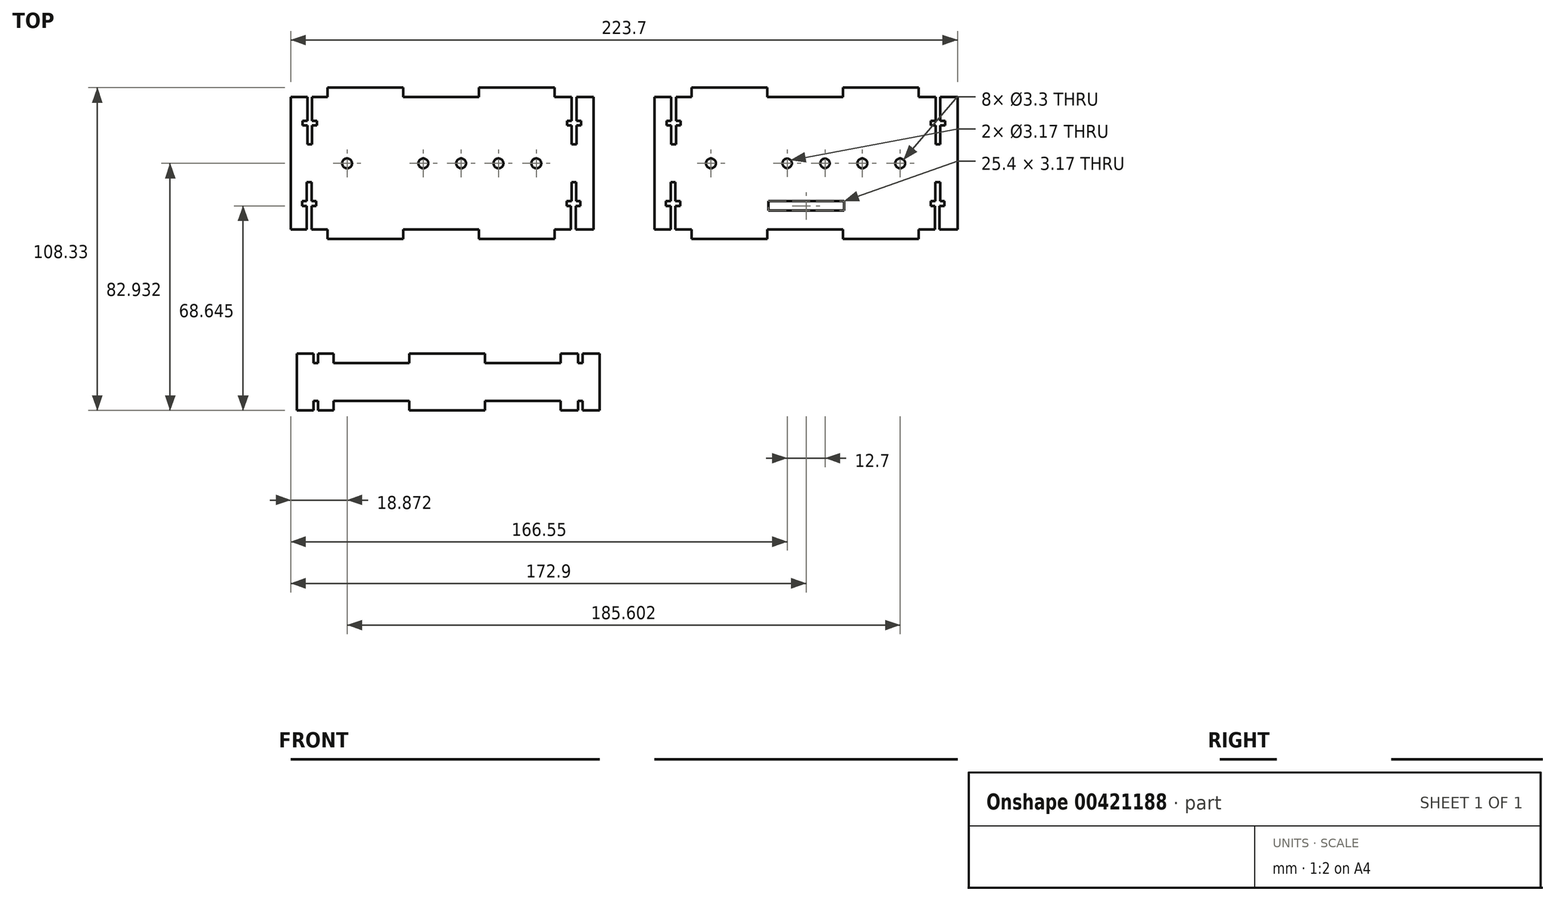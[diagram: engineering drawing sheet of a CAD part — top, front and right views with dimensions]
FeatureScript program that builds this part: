
annotation { "Feature Type Name" : "Feature", "Feature Type Description" : "" }
export const myFeature = defineFeature(function(context is Context, id is Id, definition is map)
    precondition{}
    {
        {
            var Q0;
            Q0=qCreatedBy(makeId("Top.planeOp"),FACE);
            var sketch = newSketch(context, id + "F0", { "sketchPlane" : qUnion([Q0])});
            skCircle(sketch, "E0", {"center": v(26.52, -0.26) * mm, "radius": 1.65 * mm});
            skCircle(sketch, "E1", {"center": v(90.02, -0.26) * mm, "radius": 1.65 * mm});
            skCircle(sketch, "E2", {"center": v(77.32, -0.26) * mm, "radius": 1.65 * mm});
            skLineSegment(sketch, "E3", {"start": v(19.98, -22.48) * mm, "end": v(19.98, -25.66) * mm});
            skLineSegment(sketch, "E4", {"start": v(19.98, -25.66) * mm, "end": v(45.38, -25.66) * mm});
            skLineSegment(sketch, "E5", {"start": v(70.78, -22.48) * mm, "end": v(70.78, -25.66) * mm});
            skLineSegment(sketch, "E6", {"start": v(70.78, -25.66) * mm, "end": v(96.18, -25.66) * mm});
            skLineSegment(sketch, "E7", {"start": v(45.38, -25.66) * mm, "end": v(45.38, -22.48) * mm});
            skLineSegment(sketch, "E8", {"start": v(96.18, -25.66) * mm, "end": v(96.18, -22.48) * mm});
            skLineSegment(sketch, "E9", {"start": v(7.65, -22.48) * mm, "end": v(7.65, 21.97) * mm});
            skLineSegment(sketch, "E10", {"start": v(109.25, 21.97) * mm, "end": v(109.25, -22.48) * mm});
            skLineSegment(sketch, "E11", {"start": v(45.38, 25.14) * mm, "end": v(19.98, 25.14) * mm});
            skLineSegment(sketch, "E12", {"start": v(70.78, 21.97) * mm, "end": v(70.78, 25.14) * mm});
            skLineSegment(sketch, "E13", {"start": v(70.78, 25.14) * mm, "end": v(96.18, 25.14) * mm});
            skLineSegment(sketch, "E14", {"start": v(96.18, 25.14) * mm, "end": v(96.18, 21.97) * mm});
            skLineSegment(sketch, "E15", {"start": v(45.38, 25.14) * mm, "end": v(45.38, 21.97) * mm});
            skLineSegment(sketch, "E16", {"start": v(19.98, 25.14) * mm, "end": v(19.98, 21.97) * mm});
            skLineSegment(sketch, "E17", {"start": v(45.38, -22.48) * mm, "end": v(70.78, -22.48) * mm});
            skLineSegment(sketch, "E18", {"start": v(70.78, 21.97) * mm, "end": v(45.38, 21.97) * mm});
            skLineSegment(sketch, "E19", {"start": v(13.2, 6.1) * mm, "end": v(14.8, 6.1) * mm});
            skLineSegment(sketch, "E20", {"start": v(13.2, 21.97) * mm, "end": v(7.65, 21.97) * mm});
            skLineSegment(sketch, "E21", {"start": v(14.8, 21.97) * mm, "end": v(19.98, 21.97) * mm});
            skLineSegment(sketch, "E22", {"start": v(16.38, 12.44) * mm, "end": v(16.38, 14.03) * mm});
            skLineSegment(sketch, "E23", {"start": v(11.62, 14.03) * mm, "end": v(11.62, 12.44) * mm});
            skLineSegment(sketch, "E24", {"start": v(11.62, 14.03) * mm, "end": v(13.2, 14.03) * mm});
            skLineSegment(sketch, "E25", {"start": v(16.38, 14.03) * mm, "end": v(14.8, 14.03) * mm});
            skLineSegment(sketch, "E26", {"start": v(16.38, 12.44) * mm, "end": v(14.8, 12.44) * mm});
            skLineSegment(sketch, "E27", {"start": v(11.62, 12.44) * mm, "end": v(13.2, 12.44) * mm});
            skLineSegment(sketch, "E28", {"start": v(13.2, 12.44) * mm, "end": v(13.2, 6.1) * mm});
            skLineSegment(sketch, "E29", {"start": v(13.2, 21.97) * mm, "end": v(13.2, 14.03) * mm});
            skLineSegment(sketch, "E30", {"start": v(14.8, 21.97) * mm, "end": v(14.8, 14.03) * mm});
            skLineSegment(sketch, "E31", {"start": v(14.8, 6.1) * mm, "end": v(14.8, 12.44) * mm});
            skLineSegment(sketch, "E32", {"start": v(103.52, 21.97) * mm, "end": v(103.52, 14.03) * mm});
            skLineSegment(sketch, "E33", {"start": v(103.52, 14.03) * mm, "end": v(105.1, 14.03) * mm});
            skLineSegment(sketch, "E34", {"start": v(105.1, 14.03) * mm, "end": v(105.1, 12.44) * mm});
            skLineSegment(sketch, "E35", {"start": v(105.1, 12.44) * mm, "end": v(103.52, 12.44) * mm});
            skLineSegment(sketch, "E36", {"start": v(103.52, 12.44) * mm, "end": v(103.52, 6.1) * mm});
            skLineSegment(sketch, "E37", {"start": v(103.52, 14.03) * mm, "end": v(103.52, 21.97) * mm});
            skLineSegment(sketch, "E38.top", {"start": v(103.52, 6.1) * mm, "end": v(101.93, 6.1) * mm});
            skLineSegment(sketch, "E39.bottom", {"start": v(101.93, 14.03) * mm, "end": v(100.34, 14.03) * mm});
            skLineSegment(sketch, "E39.top", {"start": v(101.93, 12.44) * mm, "end": v(100.34, 12.44) * mm});
            skLineSegment(sketch, "E39.right", {"start": v(100.34, 14.03) * mm, "end": v(100.34, 12.44) * mm});
            skLineSegment(sketch, "E40", {"start": v(101.93, 14.03) * mm, "end": v(101.93, 21.97) * mm});
            skLineSegment(sketch, "E41", {"start": v(101.93, 12.44) * mm, "end": v(101.93, 6.1) * mm});
            skLineSegment(sketch, "E42", {"start": v(103.24, -14.55) * mm, "end": v(104.82, -14.55) * mm});
            skLineSegment(sketch, "E43", {"start": v(104.82, -14.55) * mm, "end": v(104.82, -12.96) * mm});
            skLineSegment(sketch, "E44", {"start": v(104.82, -12.96) * mm, "end": v(103.43, -12.96) * mm});
            skLineSegment(sketch, "E45.bottom", {"start": v(103.43, -6.6) * mm, "end": v(101.84, -6.6) * mm});
            skLineSegment(sketch, "E46.bottom", {"start": v(101.84, -12.96) * mm, "end": v(100.25, -12.96) * mm});
            skLineSegment(sketch, "E46.top", {"start": v(101.65, -14.55) * mm, "end": v(100.25, -14.55) * mm});
            skLineSegment(sketch, "E46.right", {"start": v(100.25, -12.96) * mm, "end": v(100.25, -14.55) * mm});
            skLineSegment(sketch, "E47", {"start": v(101.84, -6.6) * mm, "end": v(101.84, -12.96) * mm});
            skLineSegment(sketch, "E48", {"start": v(103.43, -6.6) * mm, "end": v(103.43, -12.96) * mm});
            skLineSegment(sketch, "E49", {"start": v(103.24, -14.55) * mm, "end": v(103.24, -22.48) * mm});
            skLineSegment(sketch, "E50", {"start": v(101.65, -14.55) * mm, "end": v(101.65, -22.48) * mm});
            skLineSegment(sketch, "E51.top", {"start": v(13.82, -6.6) * mm, "end": v(14.61, -6.6) * mm});
            skLineSegment(sketch, "E52.bottom", {"start": v(14.61, -6.6) * mm, "end": v(13.02, -6.6) * mm});
            skLineSegment(sketch, "E53", {"start": v(13.02, -22.48) * mm, "end": v(7.65, -22.48) * mm});
            skLineSegment(sketch, "E54", {"start": v(14.61, -22.48) * mm, "end": v(19.98, -22.48) * mm});
            skLineSegment(sketch, "E55", {"start": v(14.61, -14.55) * mm, "end": v(16.2, -14.55) * mm});
            skLineSegment(sketch, "E56", {"start": v(16.2, -14.55) * mm, "end": v(16.2, -12.96) * mm});
            skLineSegment(sketch, "E57", {"start": v(16.2, -12.96) * mm, "end": v(14.61, -12.96) * mm});
            skLineSegment(sketch, "E58", {"start": v(13.02, -12.96) * mm, "end": v(11.44, -12.96) * mm});
            skLineSegment(sketch, "E59", {"start": v(11.44, -12.96) * mm, "end": v(11.44, -14.55) * mm});
            skLineSegment(sketch, "E60", {"start": v(11.44, -14.55) * mm, "end": v(13.02, -14.55) * mm});
            skLineSegment(sketch, "E61", {"start": v(13.02, -6.6) * mm, "end": v(13.02, -12.96) * mm});
            skLineSegment(sketch, "E62", {"start": v(14.61, -6.6) * mm, "end": v(14.61, -12.96) * mm});
            skLineSegment(sketch, "E63", {"start": v(14.61, -14.55) * mm, "end": v(14.61, -22.48) * mm});
            skLineSegment(sketch, "E64", {"start": v(13.02, -14.55) * mm, "end": v(13.02, -22.48) * mm});
            skLineSegment(sketch, "E65", {"start": v(96.18, -22.48) * mm, "end": v(101.65, -22.48) * mm});
            skLineSegment(sketch, "E66", {"start": v(103.24, -22.48) * mm, "end": v(109.25, -22.48) * mm});
            skPoint(sketch, "E67.endSnap0", {"position": v(70.78, 23.55) * mm});
            skLineSegment(sketch, "E68", {"start": v(45.75, -12.96) * mm, "end": v(71.15, -12.96) * mm});
            skLineSegment(sketch, "E69", {"start": v(71.15, -12.96) * mm, "end": v(71.15, -16.13) * mm});
            skLineSegment(sketch, "E70", {"start": v(45.75, -12.96) * mm, "end": v(45.75, -16.13) * mm});
            skLineSegment(sketch, "E71", {"start": v(45.75, -16.13) * mm, "end": v(71.15, -16.13) * mm});
            skCircle(sketch, "E72", {"center": v(-95.58, -0.26) * mm, "radius": 1.65 * mm});
            skCircle(sketch, "E73", {"center": v(-32.08, -0.26) * mm, "radius": 1.65 * mm});
            skCircle(sketch, "E74", {"center": v(-44.78, -0.26) * mm, "radius": 1.65 * mm});
            skLineSegment(sketch, "E75", {"start": v(-102.12, -22.48) * mm, "end": v(-102.12, -25.66) * mm});
            skLineSegment(sketch, "E76", {"start": v(-102.12, -25.66) * mm, "end": v(-76.72, -25.66) * mm});
            skLineSegment(sketch, "E77", {"start": v(-51.32, -22.48) * mm, "end": v(-51.32, -25.66) * mm});
            skLineSegment(sketch, "E78", {"start": v(-51.32, -25.66) * mm, "end": v(-25.92, -25.66) * mm});
            skLineSegment(sketch, "E79", {"start": v(-76.72, -25.66) * mm, "end": v(-76.72, -22.48) * mm});
            skLineSegment(sketch, "E80", {"start": v(-25.92, -25.66) * mm, "end": v(-25.92, -22.48) * mm});
            skLineSegment(sketch, "E81", {"start": v(-114.45, -22.48) * mm, "end": v(-114.45, 21.97) * mm});
            skLineSegment(sketch, "E82", {"start": v(-12.85, 21.97) * mm, "end": v(-12.85, -22.48) * mm});
            skLineSegment(sketch, "E83", {"start": v(-76.72, 25.14) * mm, "end": v(-102.12, 25.14) * mm});
            skLineSegment(sketch, "E84", {"start": v(-51.32, 21.97) * mm, "end": v(-51.32, 25.14) * mm});
            skLineSegment(sketch, "E85", {"start": v(-51.32, 25.14) * mm, "end": v(-25.92, 25.14) * mm});
            skLineSegment(sketch, "E86", {"start": v(-25.92, 25.14) * mm, "end": v(-25.92, 21.97) * mm});
            skLineSegment(sketch, "E87", {"start": v(-76.72, 25.14) * mm, "end": v(-76.72, 21.97) * mm});
            skLineSegment(sketch, "E88", {"start": v(-102.12, 25.14) * mm, "end": v(-102.12, 21.97) * mm});
            skLineSegment(sketch, "E89", {"start": v(-76.72, -22.48) * mm, "end": v(-51.32, -22.48) * mm});
            skLineSegment(sketch, "E90", {"start": v(-51.32, 21.97) * mm, "end": v(-76.72, 21.97) * mm});
            skLineSegment(sketch, "E91", {"start": v(-108.9, 6.1) * mm, "end": v(-107.3, 6.1) * mm});
            skLineSegment(sketch, "E92", {"start": v(-108.9, 21.97) * mm, "end": v(-114.45, 21.97) * mm});
            skLineSegment(sketch, "E93", {"start": v(-107.3, 21.97) * mm, "end": v(-102.12, 21.97) * mm});
            skLineSegment(sketch, "E94", {"start": v(-105.72, 12.44) * mm, "end": v(-105.72, 14.03) * mm});
            skLineSegment(sketch, "E95", {"start": v(-110.48, 14.03) * mm, "end": v(-110.48, 12.44) * mm});
            skLineSegment(sketch, "E96", {"start": v(-110.48, 14.03) * mm, "end": v(-108.9, 14.03) * mm});
            skLineSegment(sketch, "E97", {"start": v(-105.72, 14.03) * mm, "end": v(-107.3, 14.03) * mm});
            skLineSegment(sketch, "E98", {"start": v(-105.72, 12.44) * mm, "end": v(-107.3, 12.44) * mm});
            skLineSegment(sketch, "E99", {"start": v(-110.48, 12.44) * mm, "end": v(-108.9, 12.44) * mm});
            skLineSegment(sketch, "E100", {"start": v(-108.9, 12.44) * mm, "end": v(-108.9, 6.1) * mm});
            skLineSegment(sketch, "E101", {"start": v(-108.9, 21.97) * mm, "end": v(-108.9, 14.03) * mm});
            skLineSegment(sketch, "E102", {"start": v(-107.3, 21.97) * mm, "end": v(-107.3, 14.03) * mm});
            skLineSegment(sketch, "E103", {"start": v(-107.3, 6.1) * mm, "end": v(-107.3, 12.44) * mm});
            skLineSegment(sketch, "E104", {"start": v(-18.58, 21.97) * mm, "end": v(-18.58, 14.03) * mm});
            skLineSegment(sketch, "E105", {"start": v(-18.58, 14.03) * mm, "end": v(-17, 14.03) * mm});
            skLineSegment(sketch, "E106", {"start": v(-17, 14.03) * mm, "end": v(-17, 12.44) * mm});
            skLineSegment(sketch, "E107", {"start": v(-17, 12.44) * mm, "end": v(-18.58, 12.44) * mm});
            skLineSegment(sketch, "E108", {"start": v(-18.58, 12.44) * mm, "end": v(-18.58, 6.1) * mm});
            skLineSegment(sketch, "E109", {"start": v(-18.58, 14.03) * mm, "end": v(-18.58, 21.97) * mm});
            skLineSegment(sketch, "E110.top", {"start": v(-18.58, 6.1) * mm, "end": v(-20.17, 6.1) * mm});
            skLineSegment(sketch, "E111.bottom", {"start": v(-20.17, 14.03) * mm, "end": v(-21.76, 14.03) * mm});
            skLineSegment(sketch, "E111.top", {"start": v(-20.17, 12.44) * mm, "end": v(-21.76, 12.44) * mm});
            skLineSegment(sketch, "E111.right", {"start": v(-21.76, 14.03) * mm, "end": v(-21.76, 12.44) * mm});
            skLineSegment(sketch, "E112", {"start": v(-20.17, 14.03) * mm, "end": v(-20.17, 21.97) * mm});
            skLineSegment(sketch, "E113", {"start": v(-20.17, 12.44) * mm, "end": v(-20.17, 6.1) * mm});
            skLineSegment(sketch, "E114", {"start": v(-18.87, -14.55) * mm, "end": v(-17.28, -14.55) * mm});
            skLineSegment(sketch, "E115", {"start": v(-17.28, -14.55) * mm, "end": v(-17.28, -12.96) * mm});
            skLineSegment(sketch, "E116", {"start": v(-17.28, -12.96) * mm, "end": v(-18.68, -12.96) * mm});
            skLineSegment(sketch, "E117.bottom", {"start": v(-18.68, -6.6) * mm, "end": v(-20.26, -6.6) * mm});
            skLineSegment(sketch, "E118.bottom", {"start": v(-20.26, -12.96) * mm, "end": v(-21.85, -12.96) * mm});
            skLineSegment(sketch, "E118.top", {"start": v(-20.45, -14.55) * mm, "end": v(-21.85, -14.55) * mm});
            skLineSegment(sketch, "E118.right", {"start": v(-21.85, -12.96) * mm, "end": v(-21.85, -14.55) * mm});
            skLineSegment(sketch, "E119", {"start": v(-20.26, -6.6) * mm, "end": v(-20.26, -12.96) * mm});
            skLineSegment(sketch, "E120", {"start": v(-18.68, -6.6) * mm, "end": v(-18.68, -12.96) * mm});
            skLineSegment(sketch, "E121", {"start": v(-18.87, -14.55) * mm, "end": v(-18.87, -22.48) * mm});
            skLineSegment(sketch, "E122", {"start": v(-20.45, -14.55) * mm, "end": v(-20.45, -22.48) * mm});
            skLineSegment(sketch, "E123.top", {"start": v(-108.29, -6.6) * mm, "end": v(-107.5, -6.6) * mm});
            skLineSegment(sketch, "E124.bottom", {"start": v(-107.5, -6.6) * mm, "end": v(-109.08, -6.6) * mm});
            skLineSegment(sketch, "E125", {"start": v(-109.08, -22.48) * mm, "end": v(-114.45, -22.48) * mm});
            skLineSegment(sketch, "E126", {"start": v(-107.5, -22.48) * mm, "end": v(-102.12, -22.48) * mm});
            skLineSegment(sketch, "E127", {"start": v(-107.5, -14.55) * mm, "end": v(-105.9, -14.55) * mm});
            skLineSegment(sketch, "E128", {"start": v(-105.9, -14.55) * mm, "end": v(-105.9, -12.96) * mm});
            skLineSegment(sketch, "E129", {"start": v(-105.9, -12.96) * mm, "end": v(-107.5, -12.96) * mm});
            skLineSegment(sketch, "E130", {"start": v(-109.08, -12.96) * mm, "end": v(-110.67, -12.96) * mm});
            skLineSegment(sketch, "E131", {"start": v(-110.67, -12.96) * mm, "end": v(-110.67, -14.55) * mm});
            skLineSegment(sketch, "E132", {"start": v(-110.67, -14.55) * mm, "end": v(-109.08, -14.55) * mm});
            skLineSegment(sketch, "E133", {"start": v(-109.08, -6.6) * mm, "end": v(-109.08, -12.96) * mm});
            skLineSegment(sketch, "E134", {"start": v(-107.5, -6.6) * mm, "end": v(-107.5, -12.96) * mm});
            skLineSegment(sketch, "E135", {"start": v(-107.5, -14.55) * mm, "end": v(-107.5, -22.48) * mm});
            skLineSegment(sketch, "E136", {"start": v(-109.08, -14.55) * mm, "end": v(-109.08, -22.48) * mm});
            skLineSegment(sketch, "E137", {"start": v(-25.92, -22.48) * mm, "end": v(-20.45, -22.48) * mm});
            skLineSegment(sketch, "E138", {"start": v(-18.87, -22.48) * mm, "end": v(-12.85, -22.48) * mm});
            skPoint(sketch, "E139.endSnap0", {"position": v(-51.32, 23.55) * mm});
            skCircle(sketch, "E140", {"center": v(52.1, -0.26) * mm, "radius": 1.59 * mm});
            skCircle(sketch, "E141", {"center": v(64.8, -0.26) * mm, "radius": 1.59 * mm});
            skLineSegment(sketch, "E142", {"start": v(-25.92, 21.97) * mm, "end": v(-20.17, 21.97) * mm});
            skLineSegment(sketch, "E143", {"start": v(-18.58, 21.97) * mm, "end": v(-12.85, 21.97) * mm});
            skLineSegment(sketch, "E144", {"start": v(96.18, 21.97) * mm, "end": v(101.93, 21.97) * mm});
            skLineSegment(sketch, "E145", {"start": v(103.52, 21.97) * mm, "end": v(109.25, 21.97) * mm});
            skLineSegment(sketch, "E146", {"start": v(-74.67, -80.02) * mm, "end": v(-100.07, -80.02) * mm});
            skLineSegment(sketch, "E147", {"start": v(-49.27, -83.2) * mm, "end": v(-49.27, -80.02) * mm});
            skLineSegment(sketch, "E148", {"start": v(-49.27, -80.02) * mm, "end": v(-23.87, -80.02) * mm});
            skLineSegment(sketch, "E149", {"start": v(-23.87, -80.02) * mm, "end": v(-23.87, -83.2) * mm});
            skLineSegment(sketch, "E150", {"start": v(-74.67, -80.02) * mm, "end": v(-74.67, -83.2) * mm});
            skLineSegment(sketch, "E151", {"start": v(-100.07, -80.02) * mm, "end": v(-100.07, -83.2) * mm});
            skLineSegment(sketch, "E152", {"start": v(-49.27, -83.2) * mm, "end": v(-74.67, -83.2) * mm});
            skLineSegment(sketch, "E153", {"start": v(-106.85, -83.2) * mm, "end": v(-112.4, -83.2) * mm});
            skLineSegment(sketch, "E154", {"start": v(-105.26, -83.2) * mm, "end": v(-100.07, -83.2) * mm});
            skLineSegment(sketch, "E155", {"start": v(-100.07, -64.14) * mm, "end": v(-100.07, -67.32) * mm});
            skLineSegment(sketch, "E156", {"start": v(-100.07, -67.32) * mm, "end": v(-74.67, -67.32) * mm});
            skLineSegment(sketch, "E157", {"start": v(-74.67, -67.32) * mm, "end": v(-74.67, -64.14) * mm});
            skLineSegment(sketch, "E158", {"start": v(-49.27, -64.14) * mm, "end": v(-49.27, -67.32) * mm});
            skLineSegment(sketch, "E159", {"start": v(-49.27, -67.32) * mm, "end": v(-23.87, -67.32) * mm});
            skLineSegment(sketch, "E160", {"start": v(-23.87, -67.32) * mm, "end": v(-23.87, -64.14) * mm});
            skLineSegment(sketch, "E161", {"start": v(-74.67, -64.14) * mm, "end": v(-49.27, -64.14) * mm});
            skLineSegment(sketch, "E162", {"start": v(-112.4, -64.14) * mm, "end": v(-112.4, -83.2) * mm});
            skLineSegment(sketch, "E163", {"start": v(-10.8, -64.14) * mm, "end": v(-10.8, -83.2) * mm});
            skLineSegment(sketch, "E164", {"start": v(-105.26, -64.14) * mm, "end": v(-105.26, -67.3) * mm});
            skLineSegment(sketch, "E165", {"start": v(-105.26, -67.3) * mm, "end": v(-106.85, -67.3) * mm});
            skLineSegment(sketch, "E166", {"start": v(-106.85, -67.3) * mm, "end": v(-106.85, -64.14) * mm});
            skLineSegment(sketch, "E167", {"start": v(-18.12, -67.3) * mm, "end": v(-16.53, -67.3) * mm});
            skLineSegment(sketch, "E168", {"start": v(-16.53, -67.3) * mm, "end": v(-16.53, -64.14) * mm});
            skLineSegment(sketch, "E169", {"start": v(-18.12, -67.3) * mm, "end": v(-18.12, -64.14) * mm});
            skLineSegment(sketch, "E170", {"start": v(-16.53, -83.2) * mm, "end": v(-16.53, -80.02) * mm});
            skLineSegment(sketch, "E171", {"start": v(-16.53, -80.02) * mm, "end": v(-18.12, -80.02) * mm});
            skLineSegment(sketch, "E172", {"start": v(-18.12, -83.2) * mm, "end": v(-18.12, -80.02) * mm});
            skLineSegment(sketch, "E173", {"start": v(-106.85, -83.2) * mm, "end": v(-106.85, -80.02) * mm});
            skLineSegment(sketch, "E174", {"start": v(-106.85, -80.02) * mm, "end": v(-105.26, -80.02) * mm});
            skLineSegment(sketch, "E175", {"start": v(-105.26, -80.02) * mm, "end": v(-105.26, -83.2) * mm});
            skLineSegment(sketch, "E176", {"start": v(-18.12, -64.14) * mm, "end": v(-23.87, -64.14) * mm});
            skLineSegment(sketch, "E177", {"start": v(-16.53, -64.14) * mm, "end": v(-10.8, -64.14) * mm});
            skLineSegment(sketch, "E178", {"start": v(-10.8, -83.2) * mm, "end": v(-16.53, -83.2) * mm});
            skLineSegment(sketch, "E179", {"start": v(-18.12, -83.2) * mm, "end": v(-23.87, -83.2) * mm});
            skLineSegment(sketch, "E180", {"start": v(-106.85, -64.14) * mm, "end": v(-112.4, -64.14) * mm});
            skLineSegment(sketch, "E181", {"start": v(-105.26, -64.14) * mm, "end": v(-100.07, -64.14) * mm});
            skCircle(sketch, "E182", {"center": v(-57.3, -0.26) * mm, "radius": 1.65 * mm});
            skCircle(sketch, "E183", {"center": v(-70, -0.26) * mm, "radius": 1.65 * mm});
            skSolve(sketch);
        }
        {
            var Q0;
            Q0 = qSketchRegion(id + "F0", true);
            extrude(context, id + "F1", {"entities" : qUnion([Q0]), "depth" : 1 / 203.2 * mm});
        }
    });
